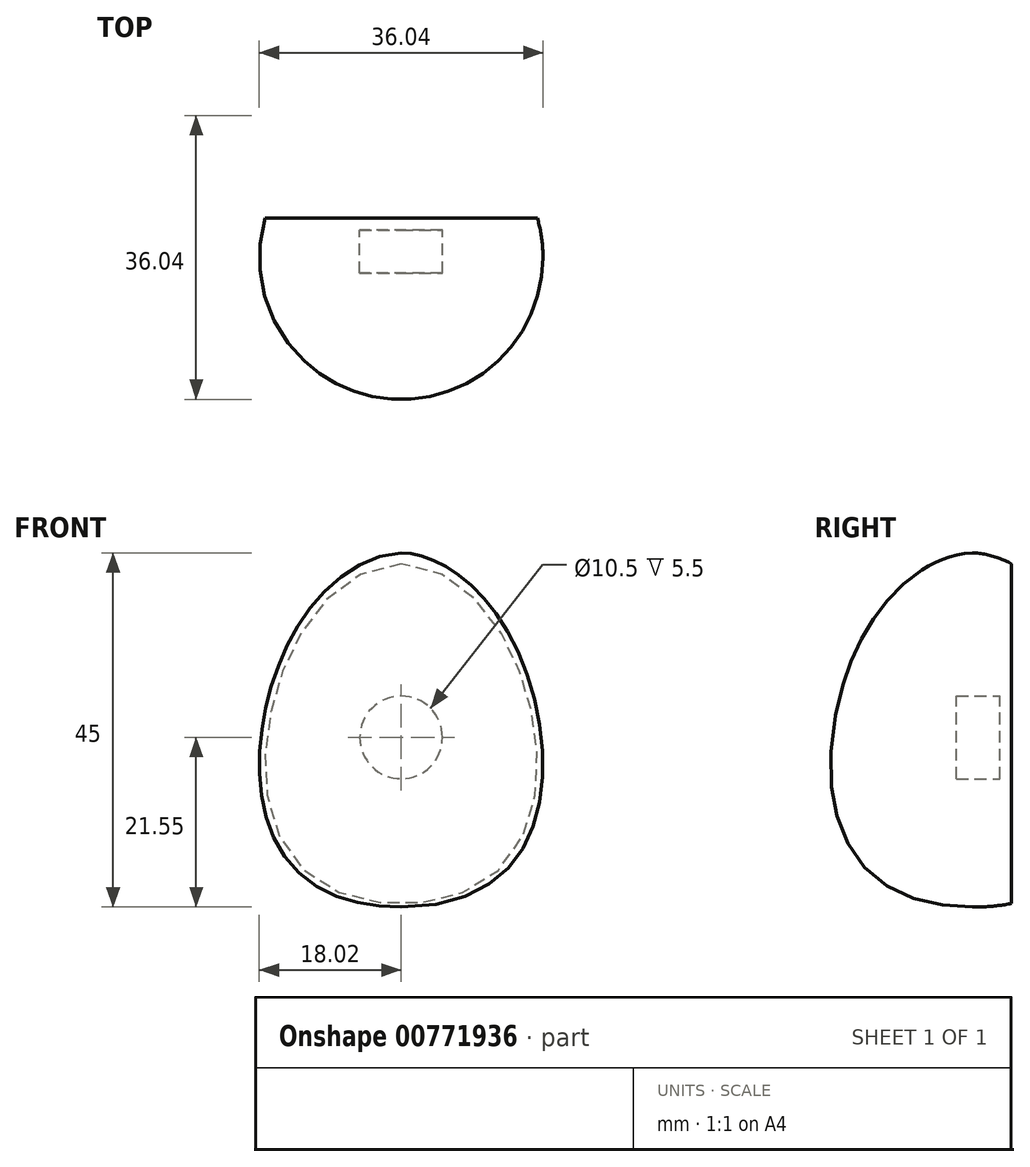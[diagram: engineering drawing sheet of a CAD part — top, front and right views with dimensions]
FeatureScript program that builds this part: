
annotation { "Feature Type Name" : "Feature", "Feature Type Description" : "" }
export const myFeature = defineFeature(function(context is Context, id is Id, definition is map)
    precondition{}
    {
        {
            var Q0;
            Q0=qCreatedBy(makeId("Front.planeOp"),FACE);
            var sketch = newSketch(context, id + "F0", { "sketchPlane" : qUnion([Q0])});
            skFitSpline(sketch, "E0", {"points": [v(0, 0) * mm, v(14.18, 33.84) * mm, v(0, 45) * mm], "startDerivative": vector(110.34, 0) * mm, "endDerivative": vector(-26.25, 0) * mm});
            skLineSegment(sketch, "E1", {"start": v(0, 0) * mm, "end": v(0, 45) * mm});
            skSolve(sketch);
        }
        {
            var Q0;
            Q0 = qSketchRegion(id + "F0", true);
            var Q1;
            Q1=sQuery(id+"F0.wireOp",EDGE,"E1");
            revolve(context, id + "F1", {"surfaceOperationType" : NewSurfaceOperationType.NEW, "entities" : qUnion([Q0]), "axis" : qUnion([Q1]), "revolveType" : RevolveType.FULL});
        }
        {
            var Q0;
            Q0=qCreatedBy(makeId("Top.planeOp"),FACE);
            var sketch = newSketch(context, id + "F2", { "sketchPlane" : qUnion([Q0])});
            skLineSegment(sketch, "E2", {"start": v(-26.36, 5) * mm, "end": v(26.87, 5) * mm});
            skLineSegment(sketch, "E3", {"start": v(26.87, 5) * mm, "end": v(26.87, 25.7) * mm});
            skLineSegment(sketch, "E4", {"start": v(26.87, 25.7) * mm, "end": v(-26.36, 25.7) * mm});
            skLineSegment(sketch, "E5", {"start": v(-26.36, 25.7) * mm, "end": v(-26.36, 5) * mm});
            skSolve(sketch);
        }
        {
            var Q0;
            Q0 = qSketchRegion(id + "F2", true);
            extrude(context, id + "F3", {"entities" : qUnion([Q0]), "operationType" : NewBodyOperationType.REMOVE, "endBound" : BoundingType.THROUGH_ALL, "depth" : 25 * mm, "offsetDistance" : 25 * mm});
        }
        {
            var Q0;
            Q0=qCreatedBy(makeId("Front.planeOp"),FACE);
            var sketch = newSketch(context, id + "F4", { "sketchPlane" : qUnion([Q0])});
            skCircle(sketch, "E6", {"center": v(0, 21.55) * mm, "radius": 5.25 * mm});
            skSolve(sketch);
        }
        {
            var Q0;
            Q0 = qSketchRegion(id + "F4", true);
            extrude(context, id + "F5", {"entities" : qUnion([Q0]), "depth" : 5.5 * mm, "offsetDistance" : 25 * mm});
        }
        {
            var Q0;
            Q0=qCreatedBy(makeId("Top.planeOp"),FACE);
            var sketch = newSketch(context, id + "F6", { "sketchPlane" : qUnion([Q0])});
            skLineSegment(sketch, "E7", {"start": v(0, 0) * mm, "end": v(0, 3.5) * mm, "construction": true});
            skSolve(sketch);
        }
        {
            var Q0;
            Q0=makeQuery(id+"F5.opExtrude","SWEPT_BODY",BODY,{"disambiguationData":[OSD([sQuery(id+"F4.wireOp",EDGE,"E6")])]});
            var Q1;
            Q1=sQuery(id+"F6.wireOp",EDGE,"E7");
            var Q2;
            Q2=qCreatedBy(makeId("Front.planeOp"),FACE);
            transform(context, id + "F7", {"entities" : qUnion([Q0]), "transformType" : TransformType.TRANSLATION_ENTITY, "oppositeDirectionEntity" : false, "transformLine" : qUnion([Q1]), "makeCopy" : false});
        }
        {
            var Q0;
            Q0=makeQuery(id+"F5.opExtrude","SWEPT_BODY",BODY,{"disambiguationData":[OSD([sQuery(id+"F4.wireOp",EDGE,"E6")])]});
            var Q1;
            Q1=makeQuery(id+"F1.opRevolve","SWEPT_BODY",BODY,{"disambiguationData":[OSD([sQuery(id+"F0.wireOp",EDGE,"E0"),sQuery(id+"F0.wireOp",EDGE,"E1")])]});
            booleanBodies(context, id + "F8", {"operationType" : BooleanOperationType.SUBTRACTION, "tools" : qUnion([Q0]), "targets" : qUnion([Q1])});
        }
    });
